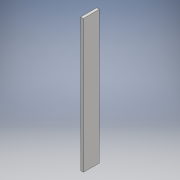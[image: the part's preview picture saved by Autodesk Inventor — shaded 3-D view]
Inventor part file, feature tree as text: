
AUTODESK INVENTOR PART (.ipt)
format: ipt  version: 2017 (Build 210142000, 142)  size: 91,136 bytes
history: native  units: mm
features: extrude x1, sketch x1
ambient origin geometry x8: Origin, YZ Plane, XZ Plane, XY Plane, X Axis, Y Axis, Z Axis, Center Point
bodies: Solid1 (feature_tree)
feature tree (2):
  extrude  "Extrusion1"  Depth=50.0mm
  sketch  "Sketch1"  dims[d0=6.0mm d1=50.0mm d2=1.0mm d3=0.0mm]
